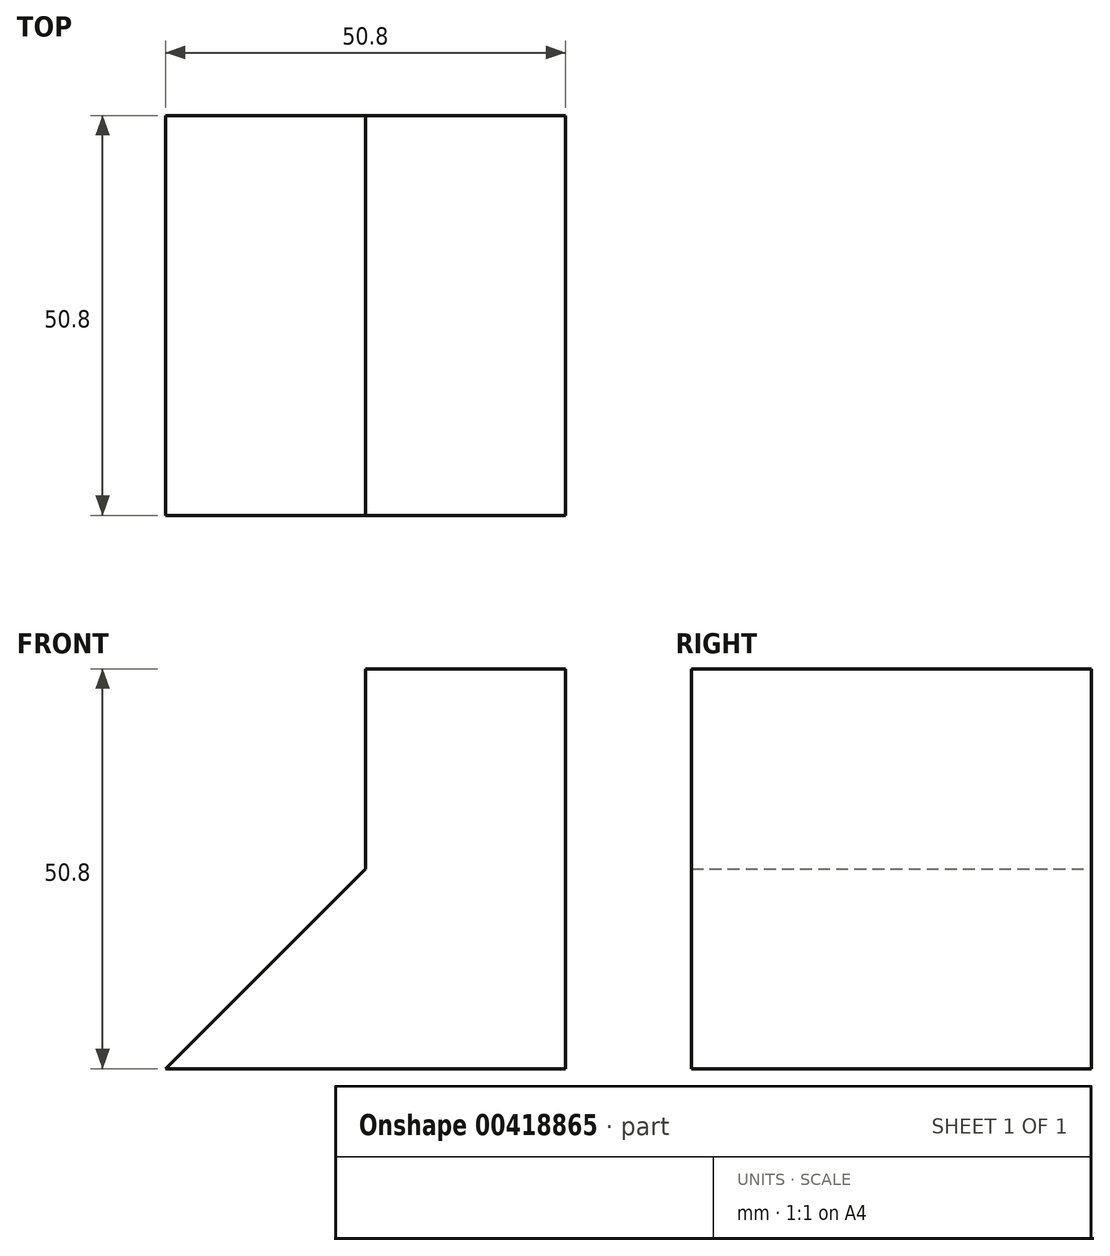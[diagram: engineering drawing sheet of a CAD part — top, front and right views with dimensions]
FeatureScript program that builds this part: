
annotation { "Feature Type Name" : "Feature", "Feature Type Description" : "" }
export const myFeature = defineFeature(function(context is Context, id is Id, definition is map)
    precondition{}
    {
        {
            var Q0;
            Q0=qCreatedBy(makeId("Front.planeOp"),FACE);
            var sketch = newSketch(context, id + "F0", { "sketchPlane" : qUnion([Q0])});
            skLineSegment(sketch, "E0", {"start": v(0, 0) * mm, "end": v(0, 50.8) * mm});
            skLineSegment(sketch, "E1", {"start": v(0, 0) * mm, "end": v(-50.8, 0) * mm});
            skLineSegment(sketch, "E2", {"start": v(0, 50.8) * mm, "end": v(-25.4, 50.8) * mm});
            skLineSegment(sketch, "E3", {"start": v(-25.4, 50.8) * mm, "end": v(-25.4, 25.4) * mm});
            skLineSegment(sketch, "E4", {"start": v(-25.4, 25.4) * mm, "end": v(-50.8, 0) * mm});
            skSolve(sketch);
        }
        {
            var Q0;
            Q0 = qSketchRegion(id + "F0", true);
            extrude(context, id + "F1", {"entities" : qUnion([Q0]), "depth" : 50.8 * mm});
        }
    });
